# Revit family: LOIRWVRP-LWO
name_source: partatom
category: Communication Devices
revit_build: Autodesk Revit 2014 (Build: 20130308_1515(x64)
units: mm (PartAtom-declared; Revit-internal decimal feet)

## types (1)
- LOIRWVRP-LWO
    Assembly Code = D5090
    Brown = Wood (Oak)
    Certifications = UL, cUL listed, IP66, NEMA4X
    Construction = Casing – Rugged, high-impact, injection-molded plastic KJB ABS Cycolac (UL-945VA)
Color-coded leads are 6” long (152.4mm)
    Coverage = LOIR-LWO: 1,600 square feet (487.68 square meters)
    Default Elevation = 48 "
    Description = The LightOWL Passive Infrared Outdoor Sensor sensor uses passive infrared (PIR)
technology to turn lighting on and off based on occupancy. Designed specifically
for areas with long-range major-motion activity, this sensor features Hubbell
Controls' patented IntelliDAPT® technology, which makes all the sensor adjustments
automatically.
    Features = IntelliDAPT self-adaptive technology—no manual
 adjustment required
• All-digital dual technology passive infrared [PIR] sensor
• Non-volatile memory for sensor settings
• 1,600 square-foot coverage area
• Relay and photocell control
• UL and cUL listed
• California Title 24 compliant
• Five-year limited warranty
• Low voltage device: 24 Vdc
• Operating temperature range from -40°F to 149°F (-40°C to 65°C)
• Outdoor rated
    Housing Material = Metal-Hubbell-Gray
    Manufacturer = Hubbell Control Solutions
    Model = LOIRWVRP-LWO
    Power Requirements = 24VDC, 33mA (uses UVPP and MP- Series power pack- not included)
    Product Documentation Link = https://hubbellcdn.com
    Product Page URL = https://www.hubbell.com
    Sensing Element = Glass - Hubbell - White
    Type Comments = CEILING AND WALL MOUNT OCCUPANCY SENSORS
    URL = https://www.hubbell.com
    Warranty = 5-Years Warranty
    Width = 4.5 "

## geometry (parser evidence)
native form markers: Sweep x1
no freeform markers — native parametric forms only
